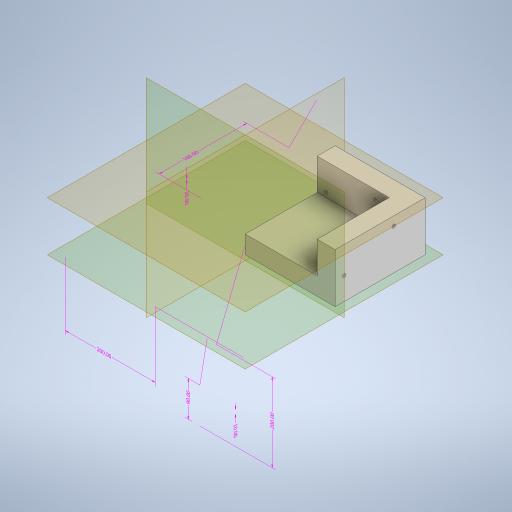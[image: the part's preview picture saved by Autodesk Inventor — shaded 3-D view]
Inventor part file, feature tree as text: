
AUTODESK INVENTOR PART (.ipt)
format: ipt  version: 2023 (Build 270158000, 158)  size: 440,832 bytes
history: native  units: mm
features: sketch x9, other x8, extrude x5, hole x4, plane x4, split x4
ambient origin geometry x8: Origin, YZ Plane, XZ Plane, XY Plane, X Axis, Y Axis, Z Axis, Center Point
bodies: Body1 (feature_tree)
feature tree (34):
  other  "Sólido1"
  other  "Anotaciones"
  extrude  "Extrusión1"  Depth=200.0mm
  hole  "Agujero1"  [1 undecoded]
  extrude  "Extrusión2"  Depth=15.0mm
  extrude  "Extrusión3"  Depth=80.0mm TaperAngle=0.0deg
  extrude  "Extrusión4"  Depth=200.0mm
  extrude  "Extrusión5"  Depth=20.0mm
  hole  "Agujero2"  [1 undecoded]
  plane  "Plano de trabajo1"
  split  "Dividir1"
  plane  "Plano de trabajo2"
  plane  "Plano de trabajo3"
  plane  "Plano de trabajo4"
  hole  "Agujero3"  [1 undecoded]
  hole  "Agujero4"  [1 undecoded]
  split  "Dividir2"
  split  "Dividir3"
  split  "Dividir4"
  sketch  "Boceto2"  dims[d7=15.0mm d8=200.0mm]
  sketch  "Boceto3"  dims[d9=10.0mm d10=0.0mm]
  sketch  "Boceto4"  dims[d11=3.5mm d12=1.75mm d13=1.75mm d14=1.75mm d15=1.75mm d16=10.0mm d17=10.0mm d19=40.0mm]
  sketch  "Boceto5"  dims[d20=3.5mm d21=6.0mm d22=4.0mm d23=2.0mm d24=90.0deg d25=8.0mm d26=20.594885mm d27=15.0mm]
  sketch  "Boceto6"  dims[d28=20.0mm d29=80.0mm d30=0.0mm]
  sketch  "Boceto7"  dims[d31=57.0mm d32=200.0mm]
  sketch  "Boceto8"  dims[d33=110.0mm d34=0.0mm d36=20.0mm]
  sketch  "Boceto9"  dims[d37=20.0mm d38=20.0mm]
  sketch  "Boceto10"  dims[d39=90.0mm d40=0.0mm d43=30.0mm d44=0.0mm d45=3.5mm d46=1.75mm d47=1.75mm d48=1.75mm d49=1.75mm d50=10.0mm d51=10.0mm d52=15.0mm d53=10.0mm d54=10.0mm d55=15.0mm d56=3.5mm d57=6.0mm d58=4.0mm d59=2.0mm d60=90.0deg d61=8.0mm d62=20.594885mm d63=10.0mm d65=10.0mm d75=200.0mm d76=10.0mm d77=20.0mm d81=40.0mm d88=90.0deg d89=10.0mm d90=30.0mm d91=5.0mm d92=5.0mm d93=5.0mm d94=5.0mm d95=30.0mm d96=5.0mm d97=5.0mm d98=3.5mm d99=5.0mm d100=5.0mm d101=5.0mm d102=5.0mm d103=5.0mm d104=20.0mm d105=3.5mm d106=6.0mm d107=4.0mm d108=2.0mm d109=90.0deg d110=8.0mm d111=20.594885mm d112=10.0mm d113=30.0mm d114=5.0mm d115=5.0mm d116=5.0mm d117=5.0mm d118=5.0mm d119=5.0mm d120=3.5mm d121=5.0mm d122=5.0mm d123=5.0mm d124=5.0mm d125=5.0mm d126=30.0mm d127=30.0mm d128=3.5mm d129=6.0mm d130=4.0mm d131=2.0mm d132=90.0deg d133=8.0mm d134=20.594885mm d66=5.760865mm d67=7.72461mm d68=200.0mm d69=3.008686mm d70=2.422102mm d71=10.0mm d72=3.500509mm d73=2.402572mm d74=90.0mm d78=3.13122mm d79=6.269346mm d80=200.0mm d82=8.450127mm d83=0.968417mm d84=20.0mm d85=4.759975mm d86=4.646891mm d87=160.0mm]
  other  "Cota lineal 1"
  other  "Cota lineal 2"
  other  "Cota lineal 3"
  other  "Cota lineal 4"
  other  "Cota lineal 5"
  other  "Cota lineal 6"
note: 4 required parameter values undecoded (feature->parameter linkage not recoverable at this tier; creation-order binding heuristic only, values carry confidence <= 0.55)
